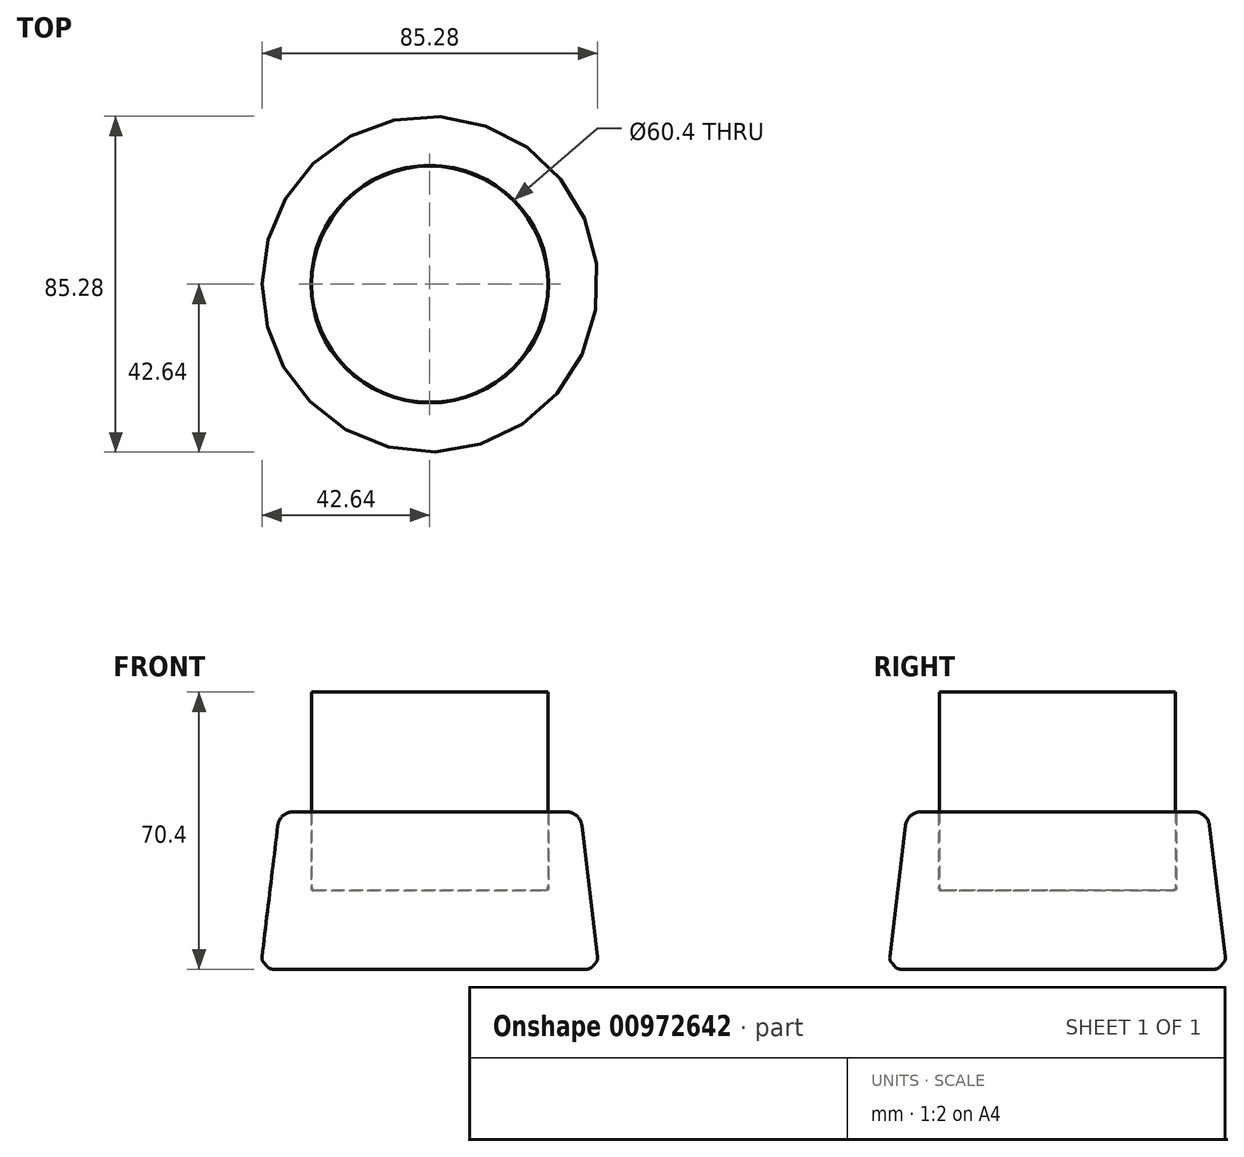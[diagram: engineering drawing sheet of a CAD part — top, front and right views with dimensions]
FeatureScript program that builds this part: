
annotation { "Feature Type Name" : "Feature", "Feature Type Description" : "" }
export const myFeature = defineFeature(function(context is Context, id is Id, definition is map)
    precondition{}
    {
        {
            var Q0;
            Q0=qCreatedBy(makeId("Front.planeOp"),FACE);
            var sketch = newSketch(context, id + "F0", { "sketchPlane" : qUnion([Q0])});
            skLineSegment(sketch, "E0", {"start": v(0, 0) * mm, "end": v(43, 0) * mm});
            skLineSegment(sketch, "E1", {"start": v(0, 0) * mm, "end": v(0, 20) * mm});
            skLineSegment(sketch, "E2", {"start": v(0, 20) * mm, "end": v(30.2, 20) * mm});
            skLineSegment(sketch, "E3", {"start": v(30.2, 20) * mm, "end": v(30.2, 40) * mm});
            skLineSegment(sketch, "E4", {"start": v(30.2, 40) * mm, "end": v(38.2, 40) * mm});
            skLineSegment(sketch, "E5", {"start": v(38.2, 40) * mm, "end": v(43, 0) * mm});
            skSolve(sketch);
        }
        {
            var Q0;
            Q0=makeQuery(id+"F0.imprint","IMPRINT",FACE,{"disambiguationData":[TD([[makeQuery(id+"F0.imprint","IMPRINT",EDGE,{"derivedFrom":sQuery(id+"F0.wireOp",EDGE,"E0")}),1.0]])]});
            var Q1;
            Q1=sQuery(id+"F0.wireOp",EDGE,"E1");
            revolve(context, id + "F1", {"surfaceOperationType" : NewSurfaceOperationType.NEW, "entities" : qUnion([Q0]), "axis" : qUnion([Q1]), "revolveType" : RevolveType.FULL});
        }
        {
            var Q0;
            Q0=makeQuery(id+"F1.opRevolve","SWEPT_EDGE",EDGE,{"disambiguationData":[OSD([sQuery(id+"F0.wireOp",EDGE,"E0"),sQuery(id+"F0.wireOp",EDGE,"E5")])]});
            chamfer(context, id + "F2", {"entities" : qUnion([Q0]), "width" : 2 * mm, "tangentPropagation" : true});
        }
        {
            var Q0;
            Q0=makeQuery(id+"F1.opRevolve","SWEPT_EDGE",EDGE,{"disambiguationData":[OSD([sQuery(id+"F0.wireOp",EDGE,"E2"),sQuery(id+"F0.wireOp",EDGE,"E3")])]});
            fillet(context, id + "F3", {"entities" : qUnion([Q0]), "radius" : .5 * mm, "tangentPropagation" : true, "allowEdgeOverflow" : false});
        }
        {
            var Q0;
            {var subQ0=sQuery(id+"F0.wireOp",EDGE,"E5");Q0=makeQuery(id+"F2.opChamfer","BLEND_EDGE",EDGE,{"blendedFrom":[makeQuery(id+"F1.opRevolve","SWEPT_EDGE",EDGE,{"disambiguationData":[OSD([sQuery(id+"F0.wireOp",EDGE,"E0"),subQ0])]}),makeQuery(id+"F1.opRevolve","SWEPT_FACE",FACE,{"disambiguationData":[OSD([subQ0])]})],"blendedInto":[makeQuery(id+"F1.opRevolve","SWEPT_FACE",FACE,{"disambiguationData":[OSD([subQ0])]})]});}
            var Q1;
            {var subQ0=sQuery(id+"F0.wireOp",EDGE,"E0");Q1=makeQuery(id+"F2.opChamfer","BLEND_EDGE",EDGE,{"blendedFrom":[makeQuery(id+"F1.opRevolve","SWEPT_EDGE",EDGE,{"disambiguationData":[OSD([subQ0,sQuery(id+"F0.wireOp",EDGE,"E5")])]}),makeQuery(id+"F1.opRevolve","SWEPT_FACE",FACE,{"disambiguationData":[OSD([subQ0])]})],"blendedInto":[makeQuery(id+"F1.opRevolve","SWEPT_FACE",FACE,{"disambiguationData":[OSD([subQ0])]})]});}
            fillet(context, id + "F4", {"entities" : qUnion([Q0, Q1]), "radius" : 2 * mm, "tangentPropagation" : true, "allowEdgeOverflow" : false});
        }
        {
            var Q0;
            Q0=makeQuery(id+"F1.opRevolve","SWEPT_EDGE",EDGE,{"disambiguationData":[OSD([sQuery(id+"F0.wireOp",EDGE,"E4"),sQuery(id+"F0.wireOp",EDGE,"E5")])]});
            fillet(context, id + "F5", {"entities" : qUnion([Q0]), "radius" : 4 * mm, "tangentPropagation" : true, "allowEdgeOverflow" : false});
        }
        {
            var Q0;
            Q0=qCreatedBy(makeId("Top.planeOp"),FACE);
            var sketch = newSketch(context, id + "F6", { "sketchPlane" : qUnion([Q0])});
            skCircle(sketch, "E6", {"center": v(0, 0) * mm, "radius": 30 * mm});
            skSolve(sketch);
        }
        {
            var Q0;
            Q0=makeQuery(id+"F6.imprint","IMPRINT",FACE,{"disambiguationData":[TD([[makeQuery(id+"F6.imprint","IMPRINT",EDGE,{"derivedFrom":sQuery(id+"F6.wireOp",EDGE,"E6")}),1.0]])]});
            extrude(context, id + "F7", {"entities" : qUnion([Q0]), "depth" : 70.4 * mm, "offsetDistance" : 25 * mm, "hasSecondDirection" : true, "secondDirectionOppositeDirection" : false, "secondDirectionDepth" : 20 * mm});
        }
        {
            var Q0;
            Q0=makeQuery(id+"F7.opExtrude","CAP_EDGE",EDGE,{"disambiguationData":[OSD([sQuery(id+"F6.wireOp",EDGE,"E6")])],"isStart":true});
            fillet(context, id + "F8", {"entities" : qUnion([Q0]), "radius" : 1 * mm, "tangentPropagation" : true, "allowEdgeOverflow" : false});
        }
        {
            var Q0;
            Q0=makeQuery(id+"F1.opRevolve","SWEPT_EDGE",EDGE,{"disambiguationData":[OSD([sQuery(id+"F0.wireOp",EDGE,"E3"),sQuery(id+"F0.wireOp",EDGE,"E4")])]});
            fillet(context, id + "F9", {"entities" : qUnion([Q0]), "radius" : .5 * mm, "tangentPropagation" : true, "allowEdgeOverflow" : false});
        }
    });
